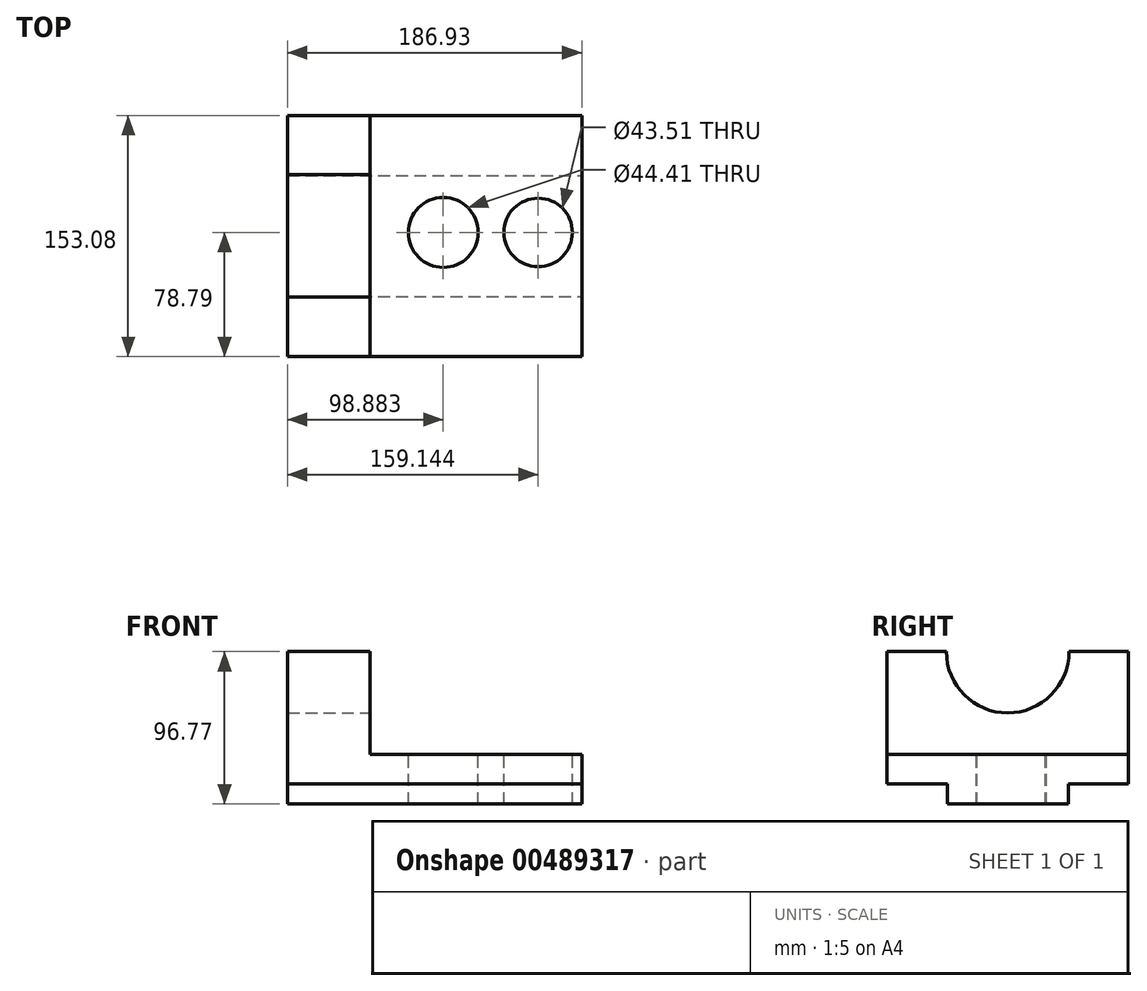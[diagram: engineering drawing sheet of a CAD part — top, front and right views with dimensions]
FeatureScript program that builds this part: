
annotation { "Feature Type Name" : "Feature", "Feature Type Description" : "" }
export const myFeature = defineFeature(function(context is Context, id is Id, definition is map)
    precondition{}
    {
        {
            var Q0;
            Q0=qCreatedBy(makeId("Top.planeOp"),FACE);
            var sketch = newSketch(context, id + "F0", { "sketchPlane" : qUnion([Q0])});
            skLineSegment(sketch, "E0.bottom", {"start": v(-111.75, 74.29) * mm, "end": v(113.28, 74.29) * mm});
            skLineSegment(sketch, "E0.top", {"start": v(-111.75, -78.79) * mm, "end": v(113.28, -78.79) * mm});
            skLineSegment(sketch, "E0.left", {"start": v(-111.75, 74.29) * mm, "end": v(-111.75, -78.79) * mm});
            skLineSegment(sketch, "E0.right", {"start": v(113.28, 74.29) * mm, "end": v(113.28, -78.79) * mm});
            skSolve(sketch);
        }
        {
            var Q0;
            Q0=makeQuery(id+"F0.imprint","IMPRINT",FACE,{"disambiguationData":[TD([[makeQuery(id+"F0.imprint","IMPRINT",EDGE,{"derivedFrom":sQuery(id+"F0.wireOp",EDGE,"E0.bottom")}),-1.0]])]});
            extrude(context, id + "F1", {"entities" : qUnion([Q0]), "depth" : 96.77 * mm});
        }
        {
            var Q0;
            Q0=makeQuery(id+"F1.opExtrude","CAP_FACE",FACE,{"disambiguationData":[OSD([sQuery(id+"F0.wireOp",EDGE,"E0.bottom"),sQuery(id+"F0.wireOp",EDGE,"E0.top"),sQuery(id+"F0.wireOp",EDGE,"E0.left"),sQuery(id+"F0.wireOp",EDGE,"E0.right")])],"isStart":false});
            var sketch = newSketch(context, id + "F2", { "sketchPlane" : qUnion([Q0])});
            skLineSegment(sketch, "E1.bottom", {"start": v(-21.27, 74.29) * mm, "end": v(113.28, 74.29) * mm});
            skLineSegment(sketch, "E1.top", {"start": v(-21.27, -78.79) * mm, "end": v(113.28, -78.79) * mm});
            skLineSegment(sketch, "E1.left", {"start": v(-21.27, 74.29) * mm, "end": v(-21.27, -78.79) * mm});
            skLineSegment(sketch, "E1.right", {"start": v(113.28, 74.29) * mm, "end": v(113.28, -78.79) * mm});
            skSolve(sketch);
        }
        {
            var Q0;
            Q0 = qSketchRegion(id + "F2", true);
            extrude(context, id + "F3", {"entities" : qUnion([Q0]), "operationType" : NewBodyOperationType.REMOVE, "oppositeDirection" : true, "depth" : 65.28 * mm});
        }
        {
            var Q0;
            Q0=makeQuery(id+"F3.boolean.opBoolean","COPY",FACE,{"derivedFrom":makeQuery(id+"F3.opExtrude","CAP_FACE",FACE,{"disambiguationData":[OSD([sQuery(id+"F2.wireOp",EDGE,"E1.bottom"),sQuery(id+"F2.wireOp",EDGE,"E1.top"),sQuery(id+"F2.wireOp",EDGE,"E1.left"),sQuery(id+"F2.wireOp",EDGE,"E1.right")])],"isStart":false})});
            var sketch = newSketch(context, id + "F4", { "sketchPlane" : qUnion([Q0])});
            skCircle(sketch, "E2", {"center": v(25.23, 0) * mm, "radius": 22.2 * mm});
            skCircle(sketch, "E3", {"center": v(85.5, 0) * mm, "radius": 21.75 * mm});
            skSolve(sketch);
        }
        {
            var Q0;
            Q0 = qSketchRegion(id + "F4", true);
            extrude(context, id + "F5", {"entities" : qUnion([Q0]), "operationType" : NewBodyOperationType.REMOVE, "oppositeDirection" : true, "depth" : 25.4 * mm});
        }
        {
            var Q0;
            Q0=makeQuery(id+"F5.boolean.opBoolean","COPY",FACE,{"derivedFrom":makeQuery(id+"F5.opExtrude","CAP_FACE",FACE,{"disambiguationData":[OSD([sQuery(id+"F4.wireOp",EDGE,"E2")])],"isStart":false})});
            var Q1;
            Q1=makeQuery(id+"F5.boolean.opBoolean","COPY",FACE,{"derivedFrom":makeQuery(id+"F5.opExtrude","CAP_FACE",FACE,{"disambiguationData":[OSD([sQuery(id+"F4.wireOp",EDGE,"E3")])],"isStart":false})});
            extrude(context, id + "F6", {"entities" : qUnion([Q0, Q1]), "operationType" : NewBodyOperationType.REMOVE, "oppositeDirection" : true, "depth" : 55.37 * mm});
        }
        {
            var Q0;
            Q0=makeQuery(id+"F1.opExtrude","SWEPT_FACE",FACE,{"disambiguationData":[OSD([sQuery(id+"F0.wireOp",EDGE,"E0.right")])]});
            var sketch = newSketch(context, id + "F7", { "sketchPlane" : qUnion([Q0])});
            skLineSegment(sketch, "E4.bottom", {"start": v(-78.79, 12.7) * mm, "end": v(-40.69, 12.7) * mm});
            skLineSegment(sketch, "E4.top", {"start": v(-78.79, 0) * mm, "end": v(-40.69, 0) * mm});
            skLineSegment(sketch, "E4.left", {"start": v(-78.79, 12.7) * mm, "end": v(-78.79, 0) * mm});
            skLineSegment(sketch, "E4.right", {"start": v(-40.69, 12.7) * mm, "end": v(-40.69, 0) * mm});
            skLineSegment(sketch, "E5.bottom", {"start": v(74.29, 12.7) * mm, "end": v(36.19, 12.7) * mm});
            skLineSegment(sketch, "E5.top", {"start": v(74.29, 0) * mm, "end": v(36.19, 0) * mm});
            skLineSegment(sketch, "E5.left", {"start": v(74.29, 12.7) * mm, "end": v(74.29, 0) * mm});
            skLineSegment(sketch, "E5.right", {"start": v(36.19, 12.7) * mm, "end": v(36.19, 0) * mm});
            skSolve(sketch);
        }
        {
            var Q0;
            Q0=makeQuery(id+"F7.imprint","IMPRINT",FACE,{"disambiguationData":[TD([[makeQuery(id+"F7.imprint","IMPRINT",EDGE,{"derivedFrom":sQuery(id+"F7.wireOp",EDGE,"E4.bottom")}),-1.0]])]});
            var Q1;
            Q1=makeQuery(id+"F7.imprint","IMPRINT",FACE,{"disambiguationData":[TD([[makeQuery(id+"F7.imprint","IMPRINT",EDGE,{"derivedFrom":sQuery(id+"F7.wireOp",EDGE,"E5.bottom")}),1.0]])]});
            extrude(context, id + "F8", {"entities" : qUnion([Q0, Q1]), "operationType" : NewBodyOperationType.REMOVE, "oppositeDirection" : true, "depth" : 261.87 * mm});
        }
        {
            var Q0;
            Q0=makeQuery(id+"F3.boolean.opBoolean","COPY",FACE,{"derivedFrom":makeQuery(id+"F3.opExtrude","SWEPT_FACE",FACE,{"disambiguationData":[OSD([sQuery(id+"F2.wireOp",EDGE,"E1.left")])]})});
            var sketch = newSketch(context, id + "F9", { "sketchPlane" : qUnion([Q0])});
            skCircle(sketch, "E6", {"center": v(-2.25, 96.77) * mm, "radius": 38.92 * mm});
            skSolve(sketch);
        }
        {
            var Q0;
            {var subQ0=sQuery(id+"F9.wireOp",EDGE,"E6");var subQ1=makeQuery(id+"F3.boolean.opBoolean","COPY",EDGE,{"derivedFrom":makeQuery(id+"F3.opExtrude","CAP_EDGE",EDGE,{"disambiguationData":[OSD([sQuery(id+"F2.wireOp",EDGE,"E1.left")])],"isStart":true})});var subQ2=makeQuery(id+"F9.imprint","INTERSECT",VERTEX,{"disambiguationData":[OD(0.0)],"derivedFrom":[subQ1,subQ0]});Q0=makeQuery(id+"F9.imprint","IMPRINT",FACE,{"disambiguationData":[TD([[makeQuery(id+"F9.imprint","IMPRINT",EDGE,{"disambiguationData":[TD([[subQ2,-1.0]])],"derivedFrom":subQ0}),1.0]])]});}
            var Q1;
            {var subQ0=sQuery(id+"F9.wireOp",EDGE,"E6");var subQ1=makeQuery(id+"F3.boolean.opBoolean","COPY",EDGE,{"derivedFrom":makeQuery(id+"F3.opExtrude","CAP_EDGE",EDGE,{"disambiguationData":[OSD([sQuery(id+"F2.wireOp",EDGE,"E1.left")])],"isStart":true})});var subQ2=makeQuery(id+"F9.imprint","INTERSECT",VERTEX,{"disambiguationData":[OD(0.0)],"derivedFrom":[subQ1,subQ0]});Q1=makeQuery(id+"F9.imprint","IMPRINT",FACE,{"disambiguationData":[TD([[makeQuery(id+"F9.imprint","IMPRINT",EDGE,{"disambiguationData":[TD([[subQ2,1.0]])],"derivedFrom":subQ0}),1.0]])]});}
            extrude(context, id + "F10", {"entities" : qUnion([Q0, Q1]), "operationType" : NewBodyOperationType.REMOVE, "oppositeDirection" : true, "depth" : 107.19 * mm});
        }
        {
            var Q0;
            Q0=makeQuery(id+"F1.opExtrude","SWEPT_FACE",FACE,{"disambiguationData":[OSD([sQuery(id+"F0.wireOp",EDGE,"E0.left")])]});
            extrude(context, id + "F11", {"entities" : qUnion([Q0]), "operationType" : NewBodyOperationType.REMOVE, "oppositeDirection" : true, "depth" : 38.1 * mm});
        }
    });
